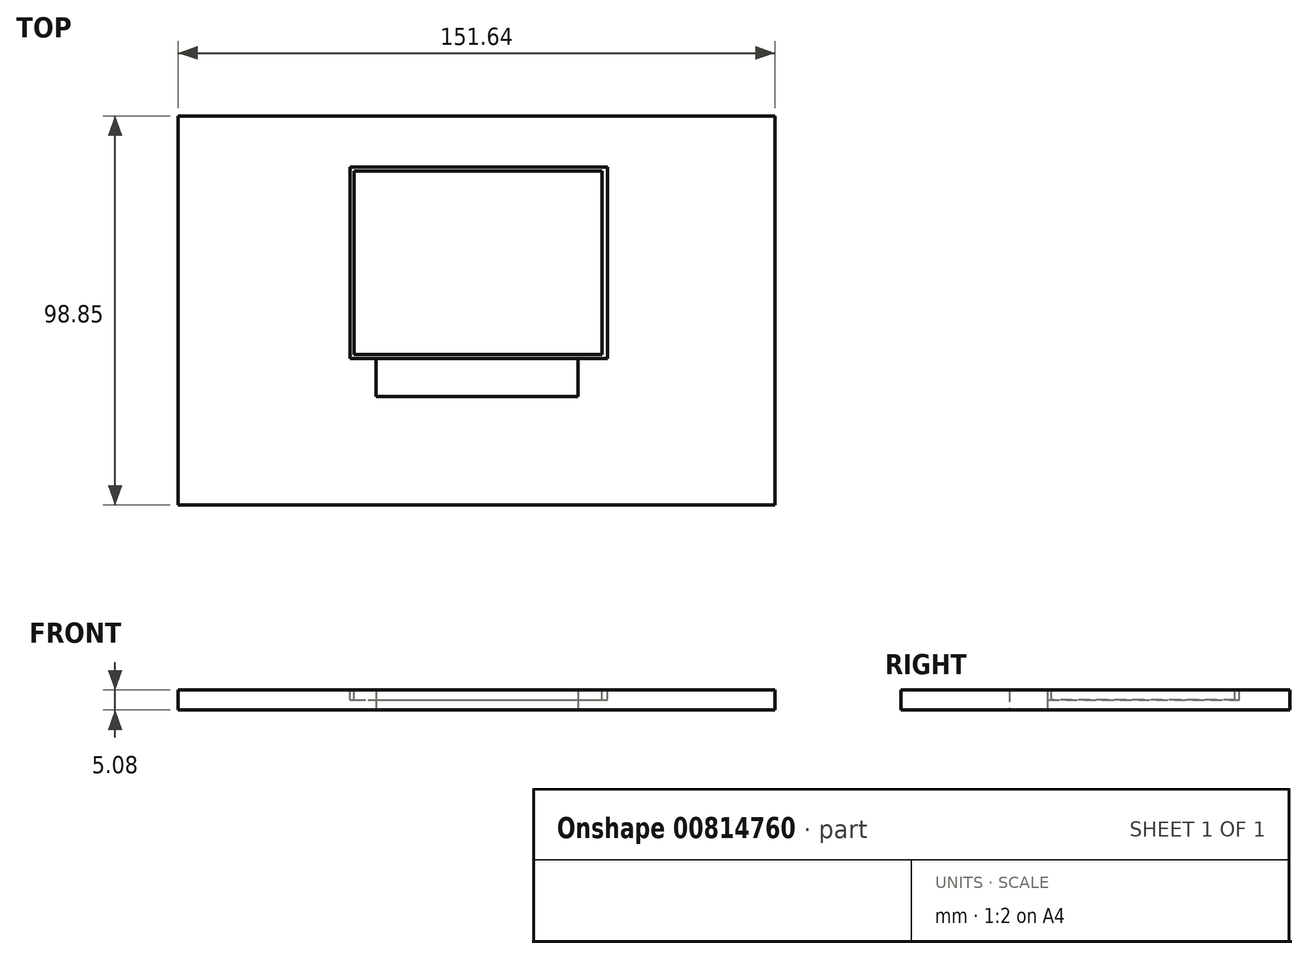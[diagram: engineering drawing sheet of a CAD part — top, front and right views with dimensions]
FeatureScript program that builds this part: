
annotation { "Feature Type Name" : "Feature", "Feature Type Description" : "" }
export const myFeature = defineFeature(function(context is Context, id is Id, definition is map)
    precondition{}
    {
        {
            var Q0;
            Q0=qCreatedBy(makeId("Top.planeOp"),FACE);
            var sketch = newSketch(context, id + "F0", { "sketchPlane" : qUnion([Q0])});
            skLineSegment(sketch, "E0.bottom", {"start": v(-75.9, 55.53) * mm, "end": v(75.74, 55.53) * mm});
            skLineSegment(sketch, "E0.top", {"start": v(-75.9, -43.32) * mm, "end": v(75.74, -43.32) * mm});
            skLineSegment(sketch, "E0.left", {"start": v(-75.9, 55.53) * mm, "end": v(-75.9, -43.32) * mm});
            skLineSegment(sketch, "E0.right", {"start": v(75.74, 55.53) * mm, "end": v(75.74, -43.32) * mm});
            skSolve(sketch);
        }
        {
            var Q0;
            Q0 = qSketchRegion(id + "F0", true);
            extrude(context, id + "F1", {"entities" : qUnion([Q0]), "depth" : 5.08 * mm, "offsetDistance" : 25.4 * mm});
        }
        {
            var Q0;
            Q0=qCreatedBy(makeId("Top.planeOp"),FACE);
            var sketch = newSketch(context, id + "F2", { "sketchPlane" : qUnion([Q0])});
            skLineSegment(sketch, "E1.bottom", {"start": v(25.65, -6.05) * mm, "end": v(-25.65, -6.05) * mm});
            skLineSegment(sketch, "E1.top", {"start": v(25.65, -15.72) * mm, "end": v(-25.65, -15.72) * mm});
            skLineSegment(sketch, "E1.left", {"start": v(25.65, -6.05) * mm, "end": v(25.65, -15.72) * mm});
            skLineSegment(sketch, "E1.right", {"start": v(-25.65, -6.05) * mm, "end": v(-25.65, -15.72) * mm});
            skPoint(sketch, "E1.middle", {"position": v(0, -10.88) * mm});
            skSolve(sketch);
        }
        {
            var Q0;
            Q0 = qSketchRegion(id + "F2", true);
            var Q1;
            Q1 = qConstructionFilter(qBodyType(qCreatedBy(id + "F2" ,EDGE), BodyType.WIRE), ConstructionObject.NO);
            extrude(context, id + "F3", {"entities" : qUnion([Q0]), "operationType" : NewBodyOperationType.REMOVE, "surfaceOperationType" : NewSurfaceOperationType.ADD, "surfaceEntities" : qUnion([Q1]), "depth" : 25.15 * mm, "offsetDistance" : 25.4 * mm});
        }
        {
            var Q0;
            Q0=makeQuery(id+"F1.opExtrude","CAP_FACE",FACE,{"disambiguationData":[OSD([sQuery(id+"F0.wireOp",EDGE,"E0.bottom"),sQuery(id+"F0.wireOp",EDGE,"E0.top"),sQuery(id+"F0.wireOp",EDGE,"E0.left"),sQuery(id+"F0.wireOp",EDGE,"E0.right")])],"isStart":false});
            var sketch = newSketch(context, id + "F4", { "sketchPlane" : qUnion([Q0])});
            skLineSegment(sketch, "E2.bottom", {"start": v(-32.28, -6.05) * mm, "end": v(33.12, -6.05) * mm});
            skLineSegment(sketch, "E2.top", {"start": v(-32.28, 42.6) * mm, "end": v(33.12, 42.6) * mm});
            skLineSegment(sketch, "E2.left", {"start": v(-32.28, -6.05) * mm, "end": v(-32.28, 42.6) * mm});
            skLineSegment(sketch, "E2.right", {"start": v(33.12, -6.05) * mm, "end": v(33.12, 42.6) * mm});
            skLineSegment(sketch, "E3.bottom", {"start": v(-31.23, 41.53) * mm, "end": v(31.8, 41.53) * mm});
            skLineSegment(sketch, "E3.top", {"start": v(-31.23, -5.05) * mm, "end": v(31.8, -5.05) * mm});
            skLineSegment(sketch, "E3.left", {"start": v(-31.23, 41.53) * mm, "end": v(-31.23, -5.05) * mm});
            skLineSegment(sketch, "E3.right", {"start": v(31.8, 41.53) * mm, "end": v(31.8, -5.05) * mm});
            skSolve(sketch);
        }
        {
            var Q0;
            Q0=makeQuery(id+"F4.imprint","IMPRINT",FACE,{"disambiguationData":[TD([[makeQuery(id+"F4.imprint","IMPRINT",EDGE,{"derivedFrom":sQuery(id+"F4.wireOp",EDGE,"E2.top")}),-1.0]])]});
            extrude(context, id + "F5", {"entities" : qUnion([Q0]), "operationType" : NewBodyOperationType.REMOVE, "oppositeDirection" : true, "depth" : 2.54 * mm, "offsetDistance" : 25.4 * mm});
        }
    });
